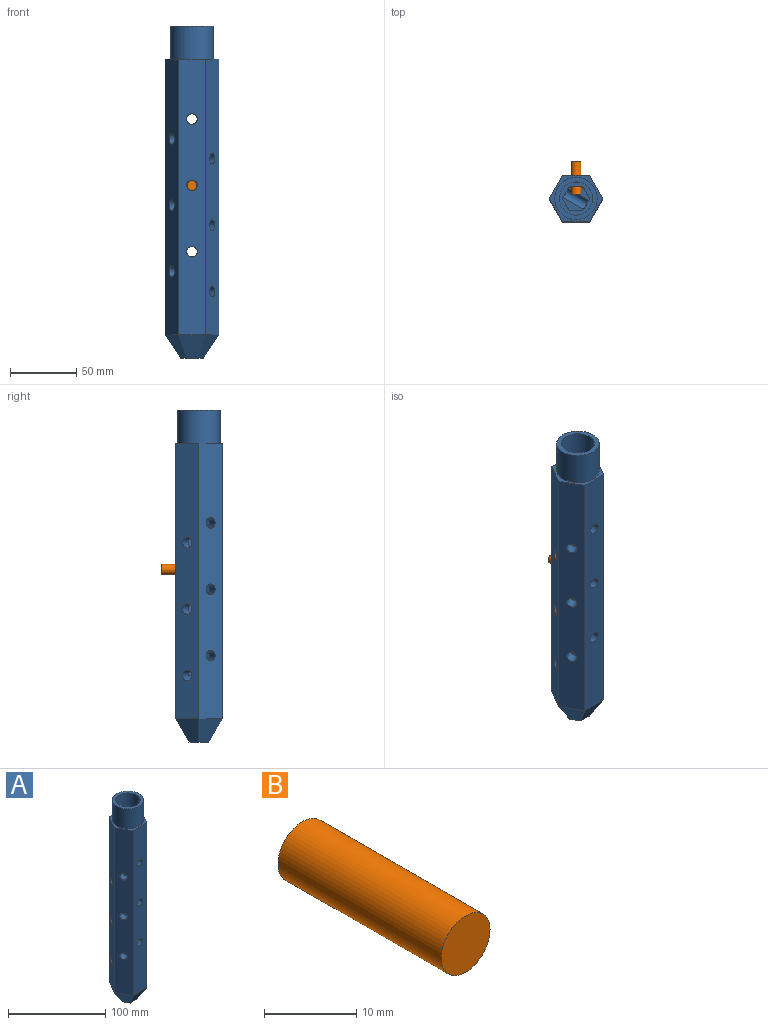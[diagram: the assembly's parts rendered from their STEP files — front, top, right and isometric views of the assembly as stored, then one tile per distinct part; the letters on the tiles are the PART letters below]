
ASSEMBLY  parts=2 mates=1
PART A: 43 faces, bbox 40.4x35x250 mm
  f0: plane 16.19x10.04mm, normal (0,0,1), area 68.3mm2, adj f19,f20,f23,f24,f38
  f1: plane 25x25mm, normal (0,0,1), area 210.3mm2, adj f17,f19,f20,f21,f22,f23,f24
  f2: plane 207.68x20.21mm, normal (0,-1,0), area 4045.8mm2, adj f3,f7,f14,f15,f29,f30,f31
  f3: plane 207.68x17.5mm, normal (0.87,-0.5,0), area 4045.8mm2, adj f2,f4,f12,f15,f38,f41,f42
  f4: plane 207.68x17.5mm, normal (0.87,0.5,0), area 4045.8mm2, adj f3,f5,f10,f15,f35,f36,f37
  f5: plane 207.68x20.21mm, normal (0,1,0), area 4045.8mm2, adj f4,f6,f9,f15,f26,f27,f28
  f6: plane 207.68x17.5mm, normal (-0.87,0.5,0), area 4045.8mm2, adj f5,f7,f11,f15,f38,f39,f40
  f7: plane 207.68x17.5mm, normal (-0.87,-0.5,0), area 4045.8mm2, adj f2,f6,f13,f15,f32,f33,f34
  f8: plane 17.32x15mm, normal (0,0,-1), area 194.9mm2, adj f9,f10,f11,f12,f13,f14
  f9: plane 20.21x17.32mm, normal (0,0.87,-0.5), area 288.7mm2, adj f5,f8,f10,f11
  f10: plane 17.5x17.32mm, normal (0.75,0.43,-0.5), area 288.7mm2, adj f4,f8,f9,f12
  f11: plane 17.5x17.32mm, normal (-0.75,0.43,-0.5), area 288.7mm2, adj f6,f8,f9,f13
  f12: plane 17.5x17.32mm, normal (0.75,-0.43,-0.5), area 288.7mm2, adj f3,f8,f10,f14
  f13: plane 17.5x17.32mm, normal (-0.75,-0.43,-0.5), area 288.7mm2, adj f7,f8,f11,f14
  f14: plane 20.21x17.32mm, normal (0,-0.87,-0.5), area 288.7mm2, adj f2,f8,f12,f13
  f15: plane 40.41x35mm, normal (0,0,1), area 256.6mm2, adj f2,f3,f4,f5,f6,f7,f16
  f16: cylinder r=16mm len=32mm, axis (0,0,1), area 2513.3mm2, adj f15,f18
  f17: cylinder r=12.5mm len=50mm, axis (0,0,1), area 3927mm2, adj f1,f18
  f18: plane 32x32mm, normal (0,0,1), area 313.4mm2, adj f16,f17
  f19: plane 150x10.39mm, normal (0,1,0), area 1408mm2, adj f0,f1,f20,f24,f29,f30,f31
  f20: plane 150x9mm, normal (-0.87,0.5,0), area 1433.2mm2, adj f0,f1,f19,f21,f25,f38,f41,f42
  f21: plane 150x9mm, normal (-0.87,-0.5,0), area 1408mm2, adj f1,f20,f22,f25,f35,f36,f37
  f22: plane 150x10.39mm, normal (0,-1,0), area 1408mm2, adj f1,f21,f23,f25,f26,f27,f28
  f23: plane 150x9mm, normal (0.87,-0.5,0), area 1433.2mm2, adj f0,f1,f22,f24,f25,f38,f39,f40
  f24: plane 150x9mm, normal (0.87,0.5,0), area 1408mm2, adj f0,f1,f19,f23,f32,f33,f34
  f25: plane 16.19x10.04mm, normal (0,0,1), area 68.3mm2, adj f20,f21,f22,f23,f38
  f26: cylinder r=4mm len=8.5mm, axis (0,-1,0), area 213.6mm2, adj f5,f22
  f27: cylinder r=4mm len=8.5mm, axis (0,-1,0), area 213.6mm2, adj f5,f22
  f28: cylinder r=4mm len=8.5mm, axis (0,-1,0), area 213.6mm2, adj f5,f22
  f29: cylinder r=4mm len=8.5mm, axis (0,-1,0), area 213.6mm2, adj f2,f19
  f30: cylinder r=4mm len=8.5mm, axis (0,-1,0), area 213.6mm2, adj f2,f19
  f31: cylinder r=4mm len=8.5mm, axis (0,-1,0), area 213.6mm2, adj f2,f19
  f32: cylinder r=4mm len=11.36mm, axis (0.87,0.5,0), area 213.6mm2, adj f7,f24
  f33: cylinder r=4mm len=11.36mm, axis (0.87,0.5,0), area 213.6mm2, adj f7,f24
  f34: cylinder r=4mm len=11.36mm, axis (0.87,0.5,0), area 213.6mm2, adj f7,f24
  f35: cylinder r=4mm len=11.36mm, axis (0.87,0.5,0), area 213.6mm2, adj f4,f21
  f36: cylinder r=4mm len=11.36mm, axis (0.87,0.5,0), area 213.6mm2, adj f4,f21
  f37: cylinder r=4mm len=11.36mm, axis (0.87,0.5,0), area 213.6mm2, adj f4,f21
  f38: cylinder r=4mm len=34.31mm, axis (0.87,-0.5,0), area 653.5mm2, adj f0,f3,f6,f20,f23,f25
  f39: cylinder r=4mm len=11.36mm, axis (0.87,-0.5,0), area 213.6mm2, adj f6,f23
  f40: cylinder r=4mm len=11.36mm, axis (0.87,-0.5,0), area 213.6mm2, adj f6,f23
  f41: cylinder r=4mm len=11.36mm, axis (0.87,-0.5,0), area 213.6mm2, adj f3,f20
  f42: cylinder r=4mm len=11.36mm, axis (0.87,-0.5,0), area 213.6mm2, adj f3,f20
PART B: 3 faces, bbox 7.5x25x7.5 mm
  f0: cylinder r=3.75mm len=25mm, axis (0,1,0), area 589mm2, adj f1,f2
  f1: plane 7.5x7.5mm, normal (0,-1,0), area 44.2mm2, adj f0
  f2: plane 7.5x7.5mm, normal (0,1,0), area 44.2mm2, adj f0
PLACE A t=(-42.13,-19.88,29.74)mm
PLACE B t=(-42.13,8.06,34.74)mm
MATE cylindrical B.f0 <-> A.f27  axis (0,1,0) through (-42.13,-4.44,34.74)mm
